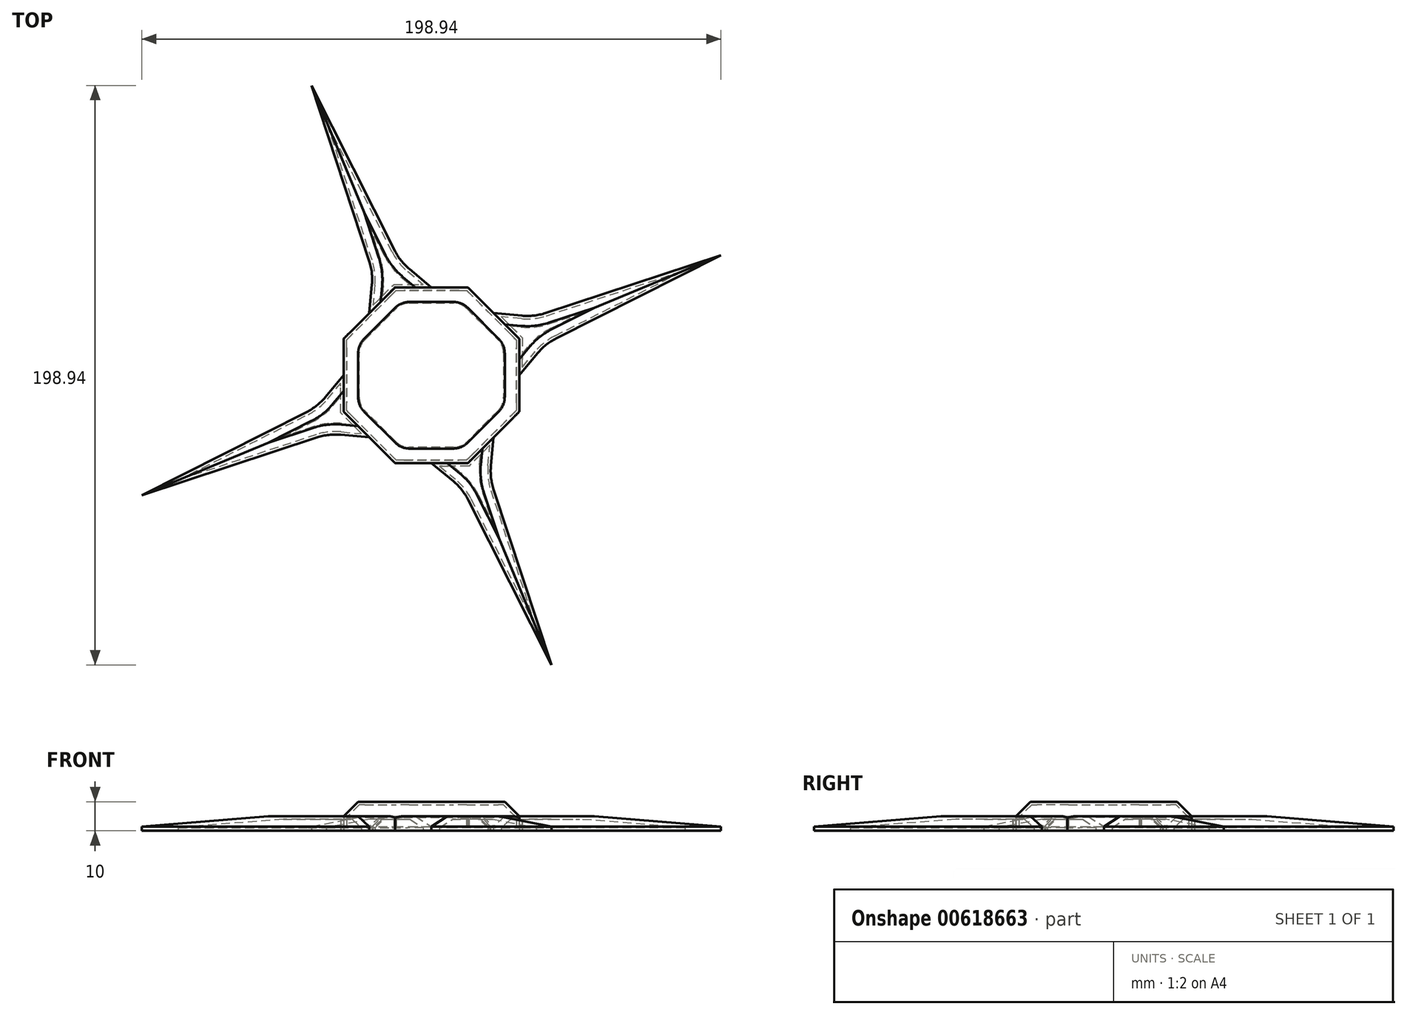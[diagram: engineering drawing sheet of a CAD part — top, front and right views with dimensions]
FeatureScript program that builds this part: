
annotation { "Feature Type Name" : "Feature", "Feature Type Description" : "" }
export const myFeature = defineFeature(function(context is Context, id is Id, definition is map)
    precondition{}
    {
        {
            var Q0;
            Q0=qCreatedBy(makeId("Top.planeOp"),FACE);
            var sketch = newSketch(context, id + "F0", { "sketchPlane" : qUnion([Q0])});
            skCircle(sketch, "E0.cCircle", {"center": v(0, 0) * mm, "radius": 30.18 * mm, "construction": true});
            skLineSegment(sketch, "E0.0", {"start": v(30.18, 12.5) * mm, "end": v(30.18, -12.5) * mm});
            skLineSegment(sketch, "E0.1", {"start": v(30.18, -12.5) * mm, "end": v(12.5, -30.18) * mm});
            skLineSegment(sketch, "E0.2", {"start": v(12.5, -30.18) * mm, "end": v(-12.5, -30.18) * mm});
            skLineSegment(sketch, "E0.3", {"start": v(-12.5, -30.18) * mm, "end": v(-30.18, -12.5) * mm});
            skLineSegment(sketch, "E0.4", {"start": v(-30.18, -12.5) * mm, "end": v(-30.18, 12.5) * mm});
            skLineSegment(sketch, "E0.5", {"start": v(-30.18, 12.5) * mm, "end": v(-12.5, 30.18) * mm});
            skLineSegment(sketch, "E0.6", {"start": v(-12.5, 30.18) * mm, "end": v(12.5, 30.18) * mm});
            skLineSegment(sketch, "E0.7", {"start": v(12.5, 30.18) * mm, "end": v(30.18, 12.5) * mm});
            skPoint(sketch, "E0.0.midPoint", {"position": v(30.18, 0) * mm});
            skPoint(sketch, "E1.endSnap0", {"position": v(-30.18, 0) * mm});
            skLineSegment(sketch, "E2", {"start": v(-12.5, 30.18) * mm, "end": v(-41.2, 99.47) * mm});
            skLineSegment(sketch, "E3", {"start": v(-30.18, -12.5) * mm, "end": v(-99.47, -41.2) * mm});
            skLineSegment(sketch, "E4", {"start": v(12.5, -30.18) * mm, "end": v(41.2, -99.47) * mm});
            skLineSegment(sketch, "E5", {"start": v(30.18, 12.5) * mm, "end": v(99.47, 41.2) * mm});
            skPoint(sketch, "E6", {"position": v(-21.34, 21.34) * mm});
            skPoint(sketch, "E7", {"position": v(-12.5, 30.18) * mm});
            skPoint(sketch, "E8", {"position": v(0, 30.18) * mm});
            skPoint(sketch, "E9", {"position": v(-30.18, -12.5) * mm});
            skPoint(sketch, "E10", {"position": v(30.18, 12.5) * mm});
            skPoint(sketch, "E11", {"position": v(21.34, 21.34) * mm});
            skPoint(sketch, "E12", {"position": v(21.34, -21.34) * mm});
            skPoint(sketch, "E13", {"position": v(12.5, -30.18) * mm});
            skPoint(sketch, "E14", {"position": v(0, -30.18) * mm});
            skPoint(sketch, "E15", {"position": v(-21.34, -21.34) * mm});
            skPoint(sketch, "E16", {"position": v(-16.92, 25.76) * mm});
            skLineSegment(sketch, "E17", {"start": v(-16.92, 25.76) * mm, "end": v(-41.2, 99.47) * mm});
            skPoint(sketch, "E18", {"position": v(-6.25, 30.18) * mm});
            skPoint(sketch, "E19", {"position": v(25.76, 16.92) * mm});
            skPoint(sketch, "E20", {"position": v(30.18, 6.25) * mm});
            skPoint(sketch, "E21", {"position": v(16.92, -25.76) * mm});
            skPoint(sketch, "E22", {"position": v(6.25, -30.18) * mm});
            skLineSegment(sketch, "E23", {"start": v(-6.25, 30.18) * mm, "end": v(-41.2, 99.47) * mm});
            skLineSegment(sketch, "E24", {"start": v(25.76, 16.92) * mm, "end": v(99.47, 41.2) * mm});
            skLineSegment(sketch, "E25", {"start": v(30.18, 6.25) * mm, "end": v(99.47, 41.2) * mm});
            skPoint(sketch, "E26", {"position": v(-20.05, 35.26) * mm});
            skPoint(sketch, "E27", {"position": v(-10.75, 39.1) * mm});
            skLineSegment(sketch, "E28", {"start": v(-20.05, 35.26) * mm, "end": v(-21.34, 21.34) * mm});
            skLineSegment(sketch, "E29", {"start": v(-10.75, 39.1) * mm, "end": v(0, 30.18) * mm});
            skPoint(sketch, "E30", {"position": v(-30.18, -6.25) * mm});
            skPoint(sketch, "E31", {"position": v(-25.76, -16.92) * mm});
            skLineSegment(sketch, "E32", {"start": v(-99.47, -41.2) * mm, "end": v(-30.18, -6.25) * mm});
            skLineSegment(sketch, "E33", {"start": v(-25.76, -16.92) * mm, "end": v(-99.47, -41.2) * mm});
            skLineSegment(sketch, "E34", {"start": v(6.25, -30.18) * mm, "end": v(41.2, -99.47) * mm});
            skLineSegment(sketch, "E35", {"start": v(16.92, -25.76) * mm, "end": v(41.2, -99.47) * mm});
            skPoint(sketch, "E36", {"position": v(-39.1, -10.75) * mm});
            skPoint(sketch, "E37", {"position": v(-35.26, -20.05) * mm});
            skPoint(sketch, "E38", {"position": v(10.75, -39.1) * mm});
            skPoint(sketch, "E39", {"position": v(20.05, -35.26) * mm});
            skPoint(sketch, "E40", {"position": v(39.1, 10.75) * mm});
            skPoint(sketch, "E41", {"position": v(35.26, 20.05) * mm});
            skLineSegment(sketch, "E42", {"start": v(-39.1, -10.75) * mm, "end": v(-30.18, 0) * mm});
            skLineSegment(sketch, "E43", {"start": v(-35.26, -20.05) * mm, "end": v(-21.34, -21.34) * mm});
            skLineSegment(sketch, "E44", {"start": v(0, -30.18) * mm, "end": v(10.75, -39.1) * mm});
            skLineSegment(sketch, "E45", {"start": v(20.05, -35.26) * mm, "end": v(21.34, -21.34) * mm});
            skLineSegment(sketch, "E46", {"start": v(30.18, 0) * mm, "end": v(39.1, 10.75) * mm});
            skLineSegment(sketch, "E47", {"start": v(35.26, 20.05) * mm, "end": v(21.34, 21.34) * mm});
            skPoint(sketch, "E48", {"position": v(-99.47, -41.2) * mm});
            skLineSegment(sketch, "E49", {"start": v(-16.92, 25.76) * mm, "end": v(-6.25, 30.18) * mm});
            skLineSegment(sketch, "E50", {"start": v(-30.18, -6.25) * mm, "end": v(-25.76, -16.92) * mm});
            skLineSegment(sketch, "E51", {"start": v(6.25, -30.18) * mm, "end": v(16.92, -25.76) * mm});
            skLineSegment(sketch, "E52", {"start": v(30.18, 6.25) * mm, "end": v(25.76, 16.92) * mm});
            skLineSegment(sketch, "E53", {"start": v(21.34, 21.34) * mm, "end": v(30.18, 0) * mm});
            skLineSegment(sketch, "E54", {"start": v(21.34, -21.34) * mm, "end": v(0, -30.18) * mm});
            skLineSegment(sketch, "E55", {"start": v(-21.34, -21.34) * mm, "end": v(-30.18, 0) * mm});
            skLineSegment(sketch, "E56", {"start": v(-21.34, 21.34) * mm, "end": v(0, 30.18) * mm});
            skSolve(sketch);
        }
        {
            var Q0;
            {var subQ0=sQuery(id+"F0.wireOp",EDGE,"E2");Q0=makeQuery(id+"F0.imprint","IMPRINT",FACE,{"disambiguationData":[TD([[makeQuery(id+"F0.imprint","IMPRINT",EDGE,{"derivedFrom":subQ0}),1.0]])]});}
            var Q1;
            {var subQ0=sQuery(id+"F0.wireOp",EDGE,"E2");Q1=makeQuery(id+"F0.imprint","IMPRINT",FACE,{"disambiguationData":[TD([[makeQuery(id+"F0.imprint","IMPRINT",EDGE,{"derivedFrom":subQ0}),-1.0]])]});}
            var Q2;
            {var subQ0=sQuery(id+"F0.wireOp",EDGE,"E3");Q2=makeQuery(id+"F0.imprint","IMPRINT",FACE,{"disambiguationData":[TD([[makeQuery(id+"F0.imprint","IMPRINT",EDGE,{"derivedFrom":subQ0}),-1.0]])]});}
            var Q3;
            {var subQ0=sQuery(id+"F0.wireOp",EDGE,"E3");Q3=makeQuery(id+"F0.imprint","IMPRINT",FACE,{"disambiguationData":[TD([[makeQuery(id+"F0.imprint","IMPRINT",EDGE,{"derivedFrom":subQ0}),1.0]])]});}
            var Q4;
            {var subQ0=sQuery(id+"F0.wireOp",EDGE,"E4");Q4=makeQuery(id+"F0.imprint","IMPRINT",FACE,{"disambiguationData":[TD([[makeQuery(id+"F0.imprint","IMPRINT",EDGE,{"derivedFrom":subQ0}),-1.0]])]});}
            var Q5;
            {var subQ0=sQuery(id+"F0.wireOp",EDGE,"E4");Q5=makeQuery(id+"F0.imprint","IMPRINT",FACE,{"disambiguationData":[TD([[makeQuery(id+"F0.imprint","IMPRINT",EDGE,{"derivedFrom":subQ0}),1.0]])]});}
            var Q6;
            {var subQ0=sQuery(id+"F0.wireOp",EDGE,"E5");Q6=makeQuery(id+"F0.imprint","IMPRINT",FACE,{"disambiguationData":[TD([[makeQuery(id+"F0.imprint","IMPRINT",EDGE,{"derivedFrom":subQ0}),-1.0]])]});}
            var Q7;
            {var subQ0=sQuery(id+"F0.wireOp",EDGE,"E5");Q7=makeQuery(id+"F0.imprint","IMPRINT",FACE,{"disambiguationData":[TD([[makeQuery(id+"F0.imprint","IMPRINT",EDGE,{"derivedFrom":subQ0}),1.0]])]});}
            var Q8;
            {var subQ3=sQuery(id+"F0.wireOp",EDGE,"E43");Q8=makeQuery(id+"F0.imprint","IMPRINT",FACE,{"disambiguationData":[TD([[makeQuery(id+"F0.imprint","IMPRINT",EDGE,{"derivedFrom":subQ3}),1.0]])]});}
            var Q9;
            {var subQ3=sQuery(id+"F0.wireOp",EDGE,"E42");Q9=makeQuery(id+"F0.imprint","IMPRINT",FACE,{"disambiguationData":[TD([[makeQuery(id+"F0.imprint","IMPRINT",EDGE,{"derivedFrom":subQ3}),-1.0]])]});}
            var Q10;
            {var subQ3=sQuery(id+"F0.wireOp",EDGE,"E28");Q10=makeQuery(id+"F0.imprint","IMPRINT",FACE,{"disambiguationData":[TD([[makeQuery(id+"F0.imprint","IMPRINT",EDGE,{"derivedFrom":subQ3}),1.0]])]});}
            var Q11;
            {var subQ3=sQuery(id+"F0.wireOp",EDGE,"E29");Q11=makeQuery(id+"F0.imprint","IMPRINT",FACE,{"disambiguationData":[TD([[makeQuery(id+"F0.imprint","IMPRINT",EDGE,{"derivedFrom":subQ3}),-1.0]])]});}
            var Q12;
            {var subQ3=sQuery(id+"F0.wireOp",EDGE,"E47");Q12=makeQuery(id+"F0.imprint","IMPRINT",FACE,{"disambiguationData":[TD([[makeQuery(id+"F0.imprint","IMPRINT",EDGE,{"derivedFrom":subQ3}),1.0]])]});}
            var Q13;
            {var subQ3=sQuery(id+"F0.wireOp",EDGE,"E46");Q13=makeQuery(id+"F0.imprint","IMPRINT",FACE,{"disambiguationData":[TD([[makeQuery(id+"F0.imprint","IMPRINT",EDGE,{"derivedFrom":subQ3}),1.0]])]});}
            var Q14;
            {var subQ3=sQuery(id+"F0.wireOp",EDGE,"E45");Q14=makeQuery(id+"F0.imprint","IMPRINT",FACE,{"disambiguationData":[TD([[makeQuery(id+"F0.imprint","IMPRINT",EDGE,{"derivedFrom":subQ3}),1.0]])]});}
            var Q15;
            {var subQ3=sQuery(id+"F0.wireOp",EDGE,"E44");Q15=makeQuery(id+"F0.imprint","IMPRINT",FACE,{"disambiguationData":[TD([[makeQuery(id+"F0.imprint","IMPRINT",EDGE,{"derivedFrom":subQ3}),1.0]])]});}
            extrude(context, id + "F1", {"entities" : qUnion([Q0, Q1, Q2, Q3, Q4, Q5, Q6, Q7, Q8, Q9, Q10, Q11, Q12, Q13, Q14, Q15]), "depth" : 5 * mm, "offsetDistance" : 25 * mm});
        }
        {
            var Q0;
            {var subQ3=sQuery(id+"F0.wireOp",EDGE,"E50");Q0=makeQuery(id+"F0.imprint","IMPRINT",FACE,{"disambiguationData":[TD([[makeQuery(id+"F0.imprint","IMPRINT",EDGE,{"derivedFrom":subQ3}),-1.0]])]});}
            var Q1;
            {var subQ0=sQuery(id+"F0.wireOp",EDGE,"E50");Q1=makeQuery(id+"F0.imprint","IMPRINT",FACE,{"disambiguationData":[TD([[makeQuery(id+"F0.imprint","IMPRINT",EDGE,{"derivedFrom":subQ0}),1.0]])]});}
            var Q2;
            {var subQ0=sQuery(id+"F0.wireOp",EDGE,"E53");Q2=makeQuery(id+"F0.imprint","IMPRINT",FACE,{"disambiguationData":[TD([[makeQuery(id+"F0.imprint","IMPRINT",EDGE,{"derivedFrom":subQ0}),-1.0]])]});}
            var Q3;
            {var subQ0=sQuery(id+"F0.wireOp",EDGE,"E52");Q3=makeQuery(id+"F0.imprint","IMPRINT",FACE,{"disambiguationData":[TD([[makeQuery(id+"F0.imprint","IMPRINT",EDGE,{"derivedFrom":subQ0}),1.0]])]});}
            var Q4;
            {var subQ3=sQuery(id+"F0.wireOp",EDGE,"E52");Q4=makeQuery(id+"F0.imprint","IMPRINT",FACE,{"disambiguationData":[TD([[makeQuery(id+"F0.imprint","IMPRINT",EDGE,{"derivedFrom":subQ3}),-1.0]])]});}
            var Q5;
            {var subQ0=sQuery(id+"F0.wireOp",EDGE,"E51");Q5=makeQuery(id+"F0.imprint","IMPRINT",FACE,{"disambiguationData":[TD([[makeQuery(id+"F0.imprint","IMPRINT",EDGE,{"derivedFrom":subQ0}),1.0]])]});}
            var Q6;
            {var subQ3=sQuery(id+"F0.wireOp",EDGE,"E51");Q6=makeQuery(id+"F0.imprint","IMPRINT",FACE,{"disambiguationData":[TD([[makeQuery(id+"F0.imprint","IMPRINT",EDGE,{"derivedFrom":subQ3}),-1.0]])]});}
            var Q7;
            {var subQ3=sQuery(id+"F0.wireOp",EDGE,"E49");Q7=makeQuery(id+"F0.imprint","IMPRINT",FACE,{"disambiguationData":[TD([[makeQuery(id+"F0.imprint","IMPRINT",EDGE,{"derivedFrom":subQ3}),1.0]])]});}
            var Q8;
            {var subQ0=sQuery(id+"F0.wireOp",EDGE,"E49");Q8=makeQuery(id+"F0.imprint","IMPRINT",FACE,{"disambiguationData":[TD([[makeQuery(id+"F0.imprint","IMPRINT",EDGE,{"derivedFrom":subQ0}),-1.0]])]});}
            extrude(context, id + "F2", {"entities" : qUnion([Q0, Q1, Q2, Q3, Q4, Q5, Q6, Q7, Q8]), "depth" : 10 * mm, "offsetDistance" : 25 * mm});
        }
        {
            var Q0;
            Q0=makeQuery(id+"F2.opExtrude","CAP_EDGE",EDGE,{"disambiguationData":[OSD([sQuery(id+"F0.wireOp",EDGE,"E0.7")])],"isStart":false});
            var Q1;
            Q1=makeQuery(id+"F2.opExtrude","CAP_EDGE",EDGE,{"disambiguationData":[OSD([sQuery(id+"F0.wireOp",EDGE,"E0.6")])],"isStart":false});
            var Q2;
            Q2=makeQuery(id+"F2.opExtrude","CAP_EDGE",EDGE,{"disambiguationData":[OSD([sQuery(id+"F0.wireOp",EDGE,"E0.5")])],"isStart":false});
            var Q3;
            Q3=makeQuery(id+"F2.opExtrude","CAP_EDGE",EDGE,{"disambiguationData":[OSD([sQuery(id+"F0.wireOp",EDGE,"E0.4")])],"isStart":false});
            var Q4;
            Q4=makeQuery(id+"F2.opExtrude","CAP_EDGE",EDGE,{"disambiguationData":[OSD([sQuery(id+"F0.wireOp",EDGE,"E0.3")])],"isStart":false});
            var Q5;
            Q5=makeQuery(id+"F2.opExtrude","CAP_EDGE",EDGE,{"disambiguationData":[OSD([sQuery(id+"F0.wireOp",EDGE,"E0.2")])],"isStart":false});
            var Q6;
            Q6=makeQuery(id+"F2.opExtrude","CAP_EDGE",EDGE,{"disambiguationData":[OSD([sQuery(id+"F0.wireOp",EDGE,"E0.1")])],"isStart":false});
            var Q7;
            Q7=makeQuery(id+"F2.opExtrude","CAP_EDGE",EDGE,{"disambiguationData":[OSD([sQuery(id+"F0.wireOp",EDGE,"E0.0")])],"isStart":false});
            chamfer(context, id + "F3", {"entities" : qUnion([Q0, Q1, Q2, Q3, Q4, Q5, Q6, Q7]), "width" : 5 * mm, "tangentPropagation" : true});
        }
        {
            var Q0;
            Q0=makeQuery(id+"F3.opChamfer","BLEND_EDGE",EDGE,{"blendedFrom":[makeQuery(id+"F2.opExtrude","CAP_EDGE",EDGE,{"disambiguationData":[OSD([sQuery(id+"F0.wireOp",EDGE,"E0.2")])],"isStart":false}),makeQuery(id+"F2.opExtrude","CAP_EDGE",EDGE,{"disambiguationData":[OSD([sQuery(id+"F0.wireOp",EDGE,"E0.3")])],"isStart":false})],"blendedInto":[]});
            var Q1;
            Q1=makeQuery(id+"F3.opChamfer","BLEND_EDGE",EDGE,{"blendedFrom":[makeQuery(id+"F2.opExtrude","CAP_EDGE",EDGE,{"disambiguationData":[OSD([sQuery(id+"F0.wireOp",EDGE,"E0.1")])],"isStart":false}),makeQuery(id+"F2.opExtrude","CAP_EDGE",EDGE,{"disambiguationData":[OSD([sQuery(id+"F0.wireOp",EDGE,"E0.2")])],"isStart":false})],"blendedInto":[]});
            var Q2;
            Q2=makeQuery(id+"F3.opChamfer","BLEND_EDGE",EDGE,{"blendedFrom":[makeQuery(id+"F2.opExtrude","CAP_EDGE",EDGE,{"disambiguationData":[OSD([sQuery(id+"F0.wireOp",EDGE,"E0.0")])],"isStart":false}),makeQuery(id+"F2.opExtrude","CAP_EDGE",EDGE,{"disambiguationData":[OSD([sQuery(id+"F0.wireOp",EDGE,"E0.1")])],"isStart":false})],"blendedInto":[]});
            var Q3;
            Q3=makeQuery(id+"F3.opChamfer","BLEND_EDGE",EDGE,{"blendedFrom":[makeQuery(id+"F2.opExtrude","CAP_EDGE",EDGE,{"disambiguationData":[OSD([sQuery(id+"F0.wireOp",EDGE,"E0.0")])],"isStart":false}),makeQuery(id+"F2.opExtrude","CAP_EDGE",EDGE,{"disambiguationData":[OSD([sQuery(id+"F0.wireOp",EDGE,"E0.7")])],"isStart":false})],"blendedInto":[]});
            var Q4;
            Q4=makeQuery(id+"F3.opChamfer","BLEND_EDGE",EDGE,{"blendedFrom":[makeQuery(id+"F2.opExtrude","CAP_EDGE",EDGE,{"disambiguationData":[OSD([sQuery(id+"F0.wireOp",EDGE,"E0.6")])],"isStart":false}),makeQuery(id+"F2.opExtrude","CAP_EDGE",EDGE,{"disambiguationData":[OSD([sQuery(id+"F0.wireOp",EDGE,"E0.7")])],"isStart":false})],"blendedInto":[]});
            var Q5;
            Q5=makeQuery(id+"F3.opChamfer","BLEND_EDGE",EDGE,{"blendedFrom":[makeQuery(id+"F2.opExtrude","CAP_EDGE",EDGE,{"disambiguationData":[OSD([sQuery(id+"F0.wireOp",EDGE,"E0.5")])],"isStart":false}),makeQuery(id+"F2.opExtrude","CAP_EDGE",EDGE,{"disambiguationData":[OSD([sQuery(id+"F0.wireOp",EDGE,"E0.6")])],"isStart":false})],"blendedInto":[]});
            var Q6;
            Q6=makeQuery(id+"F3.opChamfer","BLEND_EDGE",EDGE,{"blendedFrom":[makeQuery(id+"F2.opExtrude","CAP_EDGE",EDGE,{"disambiguationData":[OSD([sQuery(id+"F0.wireOp",EDGE,"E0.4")])],"isStart":false}),makeQuery(id+"F2.opExtrude","CAP_EDGE",EDGE,{"disambiguationData":[OSD([sQuery(id+"F0.wireOp",EDGE,"E0.5")])],"isStart":false})],"blendedInto":[]});
            var Q7;
            Q7=makeQuery(id+"F3.opChamfer","BLEND_EDGE",EDGE,{"blendedFrom":[makeQuery(id+"F2.opExtrude","CAP_EDGE",EDGE,{"disambiguationData":[OSD([sQuery(id+"F0.wireOp",EDGE,"E0.3")])],"isStart":false}),makeQuery(id+"F2.opExtrude","CAP_EDGE",EDGE,{"disambiguationData":[OSD([sQuery(id+"F0.wireOp",EDGE,"E0.4")])],"isStart":false})],"blendedInto":[]});
            fillet(context, id + "F4", {"entities" : qUnion([Q0, Q1, Q2, Q3, Q4, Q5, Q6, Q7]), "radius" : 10 * mm, "tangentPropagation" : true, "allowEdgeOverflow" : false});
        }
        {
            var Q0;
            Q0=makeQuery(id+"F1.opExtrude","SWEPT_EDGE",EDGE,{"disambiguationData":[OSD([sQuery(id+"F0.wireOp",EDGE,"E23"),sQuery(id+"F0.wireOp",EDGE,"E29")])]});
            var Q1;
            Q1=makeQuery(id+"F1.opExtrude","SWEPT_EDGE",EDGE,{"disambiguationData":[OSD([sQuery(id+"F0.wireOp",EDGE,"E24"),sQuery(id+"F0.wireOp",EDGE,"E47")])]});
            var Q2;
            Q2=makeQuery(id+"F1.opExtrude","SWEPT_EDGE",EDGE,{"disambiguationData":[OSD([sQuery(id+"F0.wireOp",EDGE,"E17"),sQuery(id+"F0.wireOp",EDGE,"E28")])]});
            var Q3;
            Q3=makeQuery(id+"F1.opExtrude","SWEPT_EDGE",EDGE,{"disambiguationData":[OSD([sQuery(id+"F0.wireOp",EDGE,"E32"),sQuery(id+"F0.wireOp",EDGE,"E42")])]});
            var Q4;
            Q4=makeQuery(id+"F1.opExtrude","SWEPT_EDGE",EDGE,{"disambiguationData":[OSD([sQuery(id+"F0.wireOp",EDGE,"E34"),sQuery(id+"F0.wireOp",EDGE,"E44")])]});
            var Q5;
            Q5=makeQuery(id+"F1.opExtrude","SWEPT_EDGE",EDGE,{"disambiguationData":[OSD([sQuery(id+"F0.wireOp",EDGE,"E33"),sQuery(id+"F0.wireOp",EDGE,"E43")])]});
            var Q6;
            Q6=makeQuery(id+"F1.opExtrude","SWEPT_EDGE",EDGE,{"disambiguationData":[OSD([sQuery(id+"F0.wireOp",EDGE,"E35"),sQuery(id+"F0.wireOp",EDGE,"E45")])]});
            var Q7;
            Q7=makeQuery(id+"F1.opExtrude","SWEPT_EDGE",EDGE,{"disambiguationData":[OSD([sQuery(id+"F0.wireOp",EDGE,"E25"),sQuery(id+"F0.wireOp",EDGE,"E46")])]});
            fillet(context, id + "F5", {"entities" : qUnion([Q0, Q1, Q2, Q3, Q4, Q5, Q6, Q7]), "radius" : 20 * mm, "tangentPropagation" : true, "allowEdgeOverflow" : false});
        }
        {
            var Q0;
            Q0=makeQuery(id+"F1.opExtrude","CAP_EDGE",EDGE,{"disambiguationData":[OSD([sQuery(id+"F0.wireOp",EDGE,"E34")])],"isStart":false});
            var Q1;
            Q1=makeQuery(id+"F1.opExtrude","CAP_EDGE",EDGE,{"disambiguationData":[OSD([sQuery(id+"F0.wireOp",EDGE,"E35")])],"isStart":false});
            var Q2;
            Q2=makeQuery(id+"F1.opExtrude","CAP_EDGE",EDGE,{"disambiguationData":[OSD([sQuery(id+"F0.wireOp",EDGE,"E33")])],"isStart":false});
            var Q3;
            Q3=makeQuery(id+"F1.opExtrude","CAP_EDGE",EDGE,{"disambiguationData":[OSD([sQuery(id+"F0.wireOp",EDGE,"E32")])],"isStart":false});
            var Q4;
            Q4=makeQuery(id+"F1.opExtrude","CAP_EDGE",EDGE,{"disambiguationData":[OSD([sQuery(id+"F0.wireOp",EDGE,"E23")])],"isStart":false});
            var Q5;
            Q5=makeQuery(id+"F1.opExtrude","CAP_EDGE",EDGE,{"disambiguationData":[OSD([sQuery(id+"F0.wireOp",EDGE,"E17")])],"isStart":false});
            var Q6;
            Q6=makeQuery(id+"F1.opExtrude","CAP_EDGE",EDGE,{"disambiguationData":[OSD([sQuery(id+"F0.wireOp",EDGE,"E24")])],"isStart":false});
            var Q7;
            Q7=makeQuery(id+"F1.opExtrude","CAP_EDGE",EDGE,{"disambiguationData":[OSD([sQuery(id+"F0.wireOp",EDGE,"E25")])],"isStart":false});
            chamfer(context, id + "F6", {"entities" : qUnion([Q0, Q1, Q2, Q3, Q4, Q5, Q6, Q7]), "width" : 3.5 * mm, "tangentPropagation" : true});
        }
        {
            var Q0;
            Q0=makeQuery(id+"F2.opExtrude","CAP_FACE",FACE,{"disambiguationData":[OSD([sQuery(id+"F0.wireOp",EDGE,"E0.0"),sQuery(id+"F0.wireOp",EDGE,"E0.1"),sQuery(id+"F0.wireOp",EDGE,"E0.2"),sQuery(id+"F0.wireOp",EDGE,"E0.3"),sQuery(id+"F0.wireOp",EDGE,"E0.4"),sQuery(id+"F0.wireOp",EDGE,"E0.5"),sQuery(id+"F0.wireOp",EDGE,"E0.6"),sQuery(id+"F0.wireOp",EDGE,"E0.7")])],"isStart":true});
            var Q1;
            Q1=makeQuery(id+"F1.opExtrude","CAP_FACE",FACE,{"disambiguationData":[OSD([sQuery(id+"F0.wireOp",EDGE,"E0.3"),sQuery(id+"F0.wireOp",EDGE,"E0.4"),sQuery(id+"F0.wireOp",EDGE,"E32"),sQuery(id+"F0.wireOp",EDGE,"E33"),sQuery(id+"F0.wireOp",EDGE,"E42"),sQuery(id+"F0.wireOp",EDGE,"E43")])],"isStart":true});
            var Q2;
            Q2=makeQuery(id+"F1.opExtrude","CAP_FACE",FACE,{"disambiguationData":[OSD([sQuery(id+"F0.wireOp",EDGE,"E0.1"),sQuery(id+"F0.wireOp",EDGE,"E0.2"),sQuery(id+"F0.wireOp",EDGE,"E34"),sQuery(id+"F0.wireOp",EDGE,"E35"),sQuery(id+"F0.wireOp",EDGE,"E44"),sQuery(id+"F0.wireOp",EDGE,"E45")])],"isStart":true});
            var Q3;
            Q3=makeQuery(id+"F1.opExtrude","CAP_FACE",FACE,{"disambiguationData":[OSD([sQuery(id+"F0.wireOp",EDGE,"E0.0"),sQuery(id+"F0.wireOp",EDGE,"E0.7"),sQuery(id+"F0.wireOp",EDGE,"E24"),sQuery(id+"F0.wireOp",EDGE,"E25"),sQuery(id+"F0.wireOp",EDGE,"E46"),sQuery(id+"F0.wireOp",EDGE,"E47")])],"isStart":true});
            var Q4;
            Q4=makeQuery(id+"F1.opExtrude","CAP_FACE",FACE,{"disambiguationData":[OSD([sQuery(id+"F0.wireOp",EDGE,"E0.5"),sQuery(id+"F0.wireOp",EDGE,"E0.6"),sQuery(id+"F0.wireOp",EDGE,"E17"),sQuery(id+"F0.wireOp",EDGE,"E23"),sQuery(id+"F0.wireOp",EDGE,"E28"),sQuery(id+"F0.wireOp",EDGE,"E29")])],"isStart":true});
            shell(context, id + "F7", {"entities" : qUnion([Q0, Q1, Q2, Q3, Q4]), "thickness" : 1 * mm});
        }
    });
